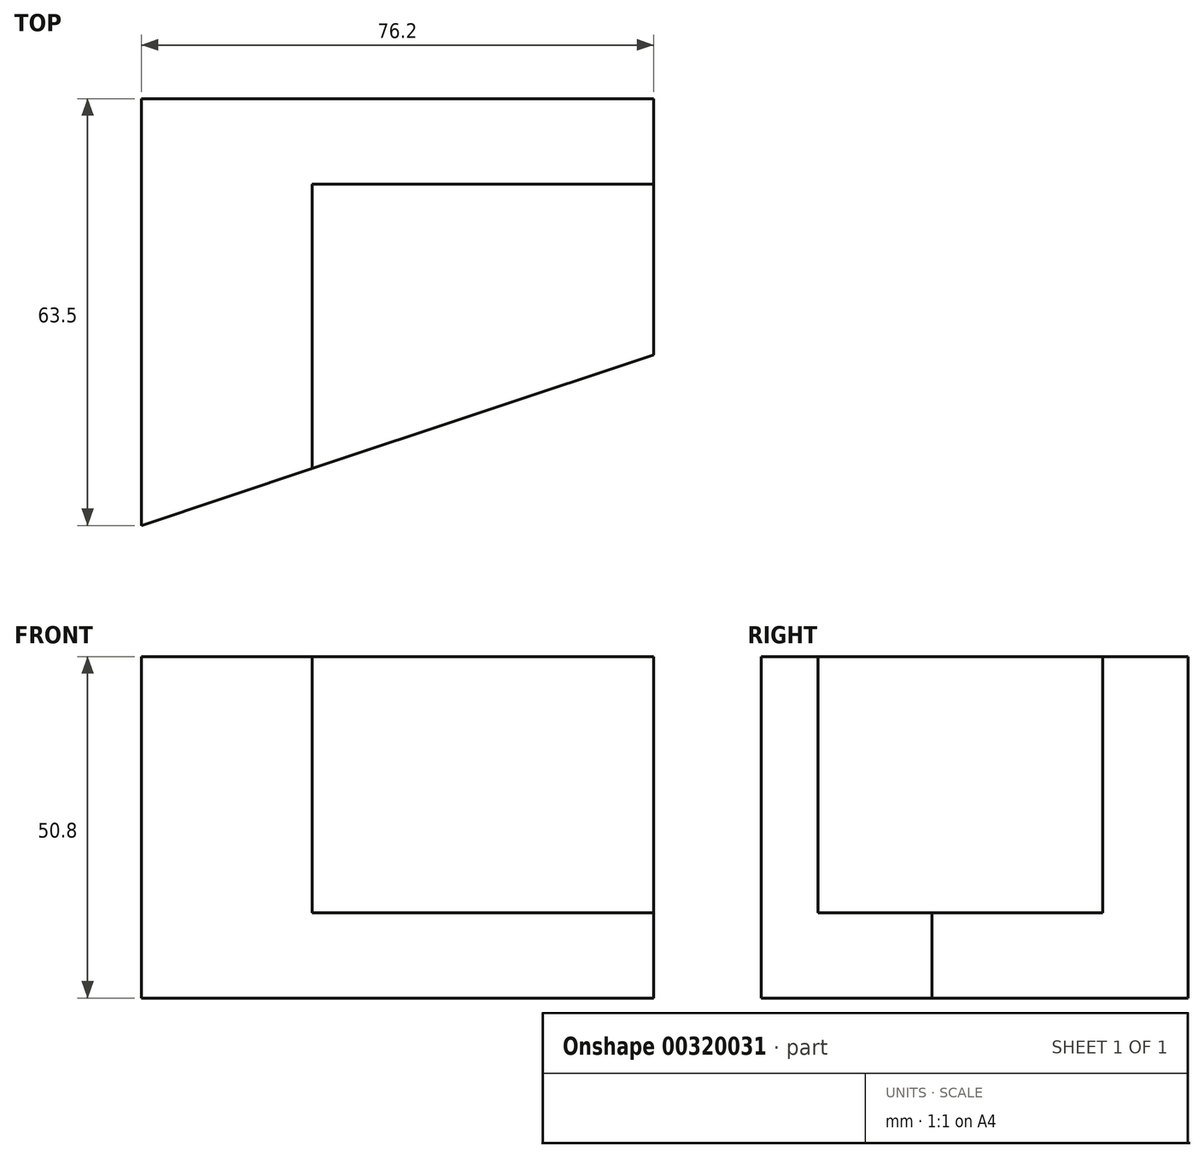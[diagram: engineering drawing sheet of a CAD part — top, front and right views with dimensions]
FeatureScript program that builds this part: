
annotation { "Feature Type Name" : "Feature", "Feature Type Description" : "" }
export const myFeature = defineFeature(function(context is Context, id is Id, definition is map)
    precondition{}
    {
        {
            var Q0;
            Q0=qCreatedBy(makeId("Top.planeOp"),FACE);
            var sketch = newSketch(context, id + "F0", { "sketchPlane" : qUnion([Q0])});
            skLineSegment(sketch, "E0", {"start": v(0, 0) * mm, "end": v(0, 63.5) * mm});
            skLineSegment(sketch, "E1", {"start": v(0, 63.5) * mm, "end": v(76.2, 63.5) * mm});
            skLineSegment(sketch, "E2", {"start": v(76.2, 63.5) * mm, "end": v(76.2, 25.4) * mm});
            skLineSegment(sketch, "E3", {"start": v(76.2, 25.4) * mm, "end": v(0, 0) * mm});
            skSolve(sketch);
        }
        {
            var Q0;
            Q0 = qSketchRegion(id + "F0", true);
            extrude(context, id + "F1", {"entities" : qUnion([Q0]), "depth" : 50.8 * mm});
        }
        {
            var Q0;
            Q0=makeQuery(id+"F1.opExtrude","CAP_FACE",FACE,{"disambiguationData":[OSD([sQuery(id+"F0.wireOp",EDGE,"E0"),sQuery(id+"F0.wireOp",EDGE,"E1"),sQuery(id+"F0.wireOp",EDGE,"E2"),sQuery(id+"F0.wireOp",EDGE,"E3")])],"isStart":false});
            var sketch = newSketch(context, id + "F2", { "sketchPlane" : qUnion([Q0])});
            skLineSegment(sketch, "E4.0.0", {"start": v(0, 0) * mm, "end": v(76.2, 25.4) * mm});
            skLineSegment(sketch, "E4.0.1", {"start": v(76.2, 25.4) * mm, "end": v(76.2, 63.5) * mm});
            skLineSegment(sketch, "E4.0.2", {"start": v(76.2, 63.5) * mm, "end": v(0, 63.5) * mm});
            skLineSegment(sketch, "E4.0.3", {"start": v(0, 63.5) * mm, "end": v(0, 0) * mm});
            skLineSegment(sketch, "E5", {"start": v(76.2, 50.8) * mm, "end": v(25.4, 50.8) * mm});
            skLineSegment(sketch, "E6", {"start": v(25.4, 50.8) * mm, "end": v(25.4, 8.47) * mm});
            skLineSegment(sketch, "E7", {"start": v(25.4, 8.47) * mm, "end": v(76.2, 25.4) * mm});
            skSolve(sketch);
        }
        {
            var Q0;
            {var subQ2=sQuery(id+"F2.wireOp",EDGE,"E5");Q0=makeQuery(id+"F2.imprint","IMPRINT",FACE,{"disambiguationData":[TD([[makeQuery(id+"F2.imprint","IMPRINT",EDGE,{"derivedFrom":subQ2}),1.0]])]});}
            extrude(context, id + "F3", {"entities" : qUnion([Q0]), "operationType" : NewBodyOperationType.REMOVE, "oppositeDirection" : true, "depth" : 38.1 * mm});
        }
    });
